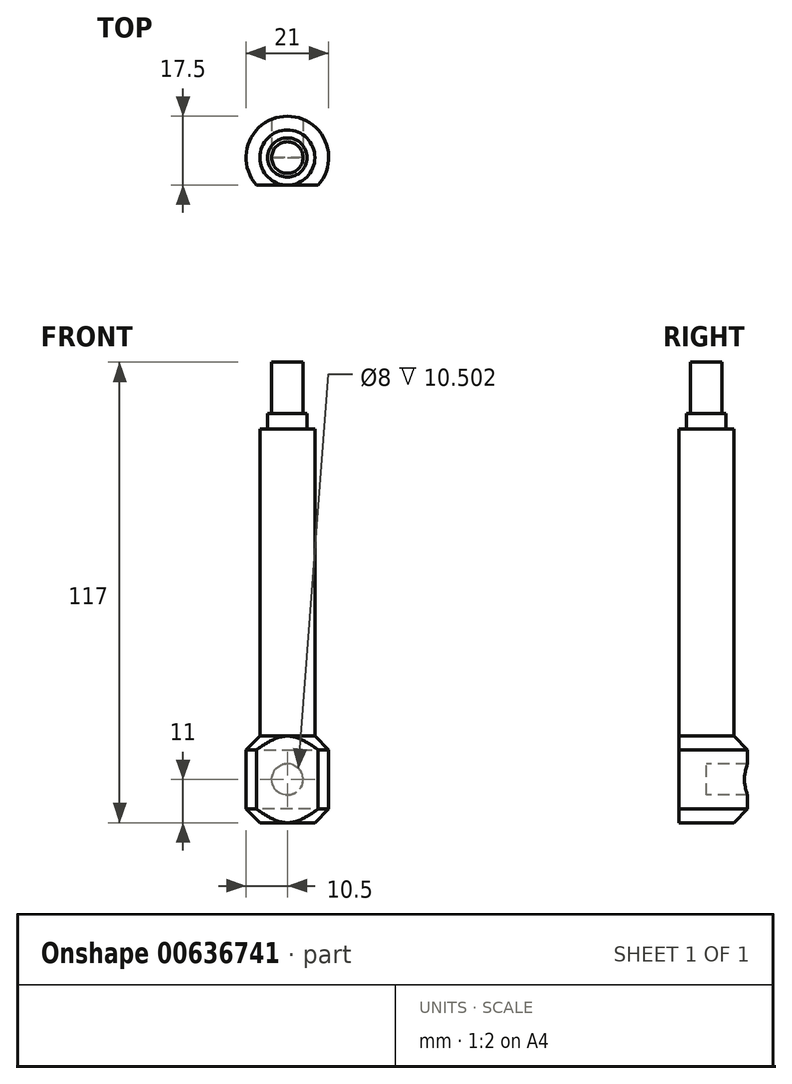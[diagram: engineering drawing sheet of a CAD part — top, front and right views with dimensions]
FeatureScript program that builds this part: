
annotation { "Feature Type Name" : "Feature", "Feature Type Description" : "" }
export const myFeature = defineFeature(function(context is Context, id is Id, definition is map)
    precondition{}
    {
        {
            var Q0;
            Q0=qCreatedBy(makeId("Front.planeOp"),FACE);
            var sketch = newSketch(context, id + "F0", { "sketchPlane" : qUnion([Q0])});
            skLineSegment(sketch, "E0", {"start": v(0, 0) * mm, "end": v(10.5, 0) * mm});
            skLineSegment(sketch, "E1", {"start": v(10.5, 0) * mm, "end": v(10.5, 22) * mm});
            skLineSegment(sketch, "E2", {"start": v(10.5, 22) * mm, "end": v(7, 22) * mm});
            skLineSegment(sketch, "E3", {"start": v(7, 22) * mm, "end": v(7, 100) * mm});
            skLineSegment(sketch, "E4", {"start": v(7, 100) * mm, "end": v(5, 100) * mm});
            skLineSegment(sketch, "E5", {"start": v(5, 100) * mm, "end": v(5, 104) * mm});
            skLineSegment(sketch, "E6", {"start": v(5, 104) * mm, "end": v(4, 104) * mm});
            skLineSegment(sketch, "E7", {"start": v(4, 104) * mm, "end": v(4, 117) * mm});
            skLineSegment(sketch, "E8", {"start": v(4, 117) * mm, "end": v(0, 117) * mm});
            skLineSegment(sketch, "E9", {"start": v(0, 117) * mm, "end": v(0, 0) * mm});
            skLineSegment(sketch, "E10", {"start": v(0, 117) * mm, "end": v(0, 0) * mm, "construction": true});
            skSolve(sketch);
        }
        {
            var Q0;
            Q0=qSketchRegion(id+"F0",true);
            var Q1;
            Q1=sQuery(id+"F0.wireOp",EDGE,"E9");
            revolve(context, id + "F1", {"entities" : qUnion([Q0]), "axis" : qUnion([Q1]), "revolveType" : RevolveType.FULL});
        }
        {
            var Q0;
            Q0=qCreatedBy(makeId("Front.planeOp"),FACE);
            var sketch = newSketch(context, id + "F2", { "sketchPlane" : qUnion([Q0])});
            skLineSegment(sketch, "E11", {"start": v(-10.5, 0) * mm, "end": v(-10.5, 22) * mm, "construction": true});
            skLineSegment(sketch, "E12", {"start": v(10.5, 22) * mm, "end": v(10.5, 0) * mm, "construction": true});
            skLineSegment(sketch, "E13", {"start": v(0, 0) * mm, "end": v(0, 28.11) * mm, "construction": true});
            skLineSegment(sketch, "E14", {"start": v(-10.5, 11) * mm, "end": v(10.5, 11) * mm, "construction": true});
            skPoint(sketch, "E15", {"position": v(0, 11) * mm});
            skSolve(sketch);
        }
        {
            var Q0;
            Q0=sQuery(id+"F2.wireOp",VERTEX,"E15");
            var Q1;
            Q1=makeQuery(id+"F1.opRevolve","SWEPT_BODY",BODY,{"disambiguationData":[OSD([sQuery(id+"F0.wireOp",EDGE,"E0"),sQuery(id+"F0.wireOp",EDGE,"E1"),sQuery(id+"F0.wireOp",EDGE,"E2"),sQuery(id+"F0.wireOp",EDGE,"E3"),sQuery(id+"F0.wireOp",EDGE,"E4"),sQuery(id+"F0.wireOp",EDGE,"E5"),sQuery(id+"F0.wireOp",EDGE,"E6"),sQuery(id+"F0.wireOp",EDGE,"E7"),sQuery(id+"F0.wireOp",EDGE,"E8"),sQuery(id+"F0.wireOp",EDGE,"E9")])]});
            hole(context, id + "F3", {"style" : HoleStyle.SIMPLE, "endStyle" : HoleEndStyle.THROUGH, "holeDiameter" : 8 * mm, "tappedDepth" : 12 * mm, "tapClearance" : 3, "locations" : qUnion([Q0]), "scope" : qUnion([Q1])});
        }
        {
            var Q0;
            Q0=qCreatedBy(makeId("Front.planeOp"),FACE);
            cPlane(context, id + "F4", {"entities" : qUnion([Q0]), "cplaneType" : CPlaneType.OFFSET, "offset" : 7 * mm, "width" : 150 * mm, "height" : 150 * mm});
        }
        {
            var Q0;
            Q0=qCreatedBy(id+"F4.planeOp",FACE);
            var sketch = newSketch(context, id + "F5", { "sketchPlane" : qUnion([Q0])});
            skLineSegment(sketch, "E16.bottom", {"start": v(-12.1, 22) * mm, "end": v(13.39, 22) * mm});
            skLineSegment(sketch, "E16.top", {"start": v(-12.1, 0) * mm, "end": v(13.39, 0) * mm});
            skLineSegment(sketch, "E16.left", {"start": v(-12.1, 22) * mm, "end": v(-12.1, 0) * mm});
            skLineSegment(sketch, "E16.right", {"start": v(13.39, 22) * mm, "end": v(13.39, 0) * mm});
            skLineSegment(sketch, "E17", {"start": v(-7.83, 0) * mm, "end": v(-7.83, 22) * mm, "construction": true});
            skLineSegment(sketch, "E18", {"start": v(7.83, 22) * mm, "end": v(7.83, 0) * mm, "construction": true});
            skLineSegment(sketch, "E19", {"start": v(0, 100) * mm, "end": v(0, 22) * mm, "construction": true});
            skLineSegment(sketch, "E20", {"start": v(-7.83, 0) * mm, "end": v(-7.83, 22) * mm});
            skLineSegment(sketch, "E21", {"start": v(7.83, 22) * mm, "end": v(7.83, 0) * mm});
            skSolve(sketch);
        }
        {
            var Q0;
            Q0=qSketchRegion(id+"F5",true);
            extrude(context, id + "F6", {"entities" : qUnion([Q0]), "operationType" : NewBodyOperationType.REMOVE, "endBound" : BoundingType.THROUGH_ALL, "depth" : 25 * mm});
        }
        {
            var Q0;
            Q0=makeQuery(id+"FCb6IwEKzA1KBKa_1.1.F6.boolean.opBoolean","SPLIT",EDGE,{"disambiguationData":[OD(1.0)],"derivedFrom":makeQuery(id+"F1.opRevolve","SWEPT_EDGE",EDGE,{"disambiguationData":[OSD([sQuery(id+"F0.wireOp",EDGE,"E1"),sQuery(id+"F0.wireOp",EDGE,"E2")])]})});
            var Q1;
            Q1=makeQuery(id+"FCb6IwEKzA1KBKa_1.1.F6.boolean.opBoolean","SPLIT",EDGE,{"disambiguationData":[OD(0.0)],"derivedFrom":makeQuery(id+"F1.opRevolve","SWEPT_EDGE",EDGE,{"disambiguationData":[OSD([sQuery(id+"F0.wireOp",EDGE,"E1"),sQuery(id+"F0.wireOp",EDGE,"E2")])]})});
            var Q2;
            Q2=makeQuery(id+"FCb6IwEKzA1KBKa_1.1.F6.boolean.opBoolean","SPLIT",EDGE,{"disambiguationData":[OD(1.0)],"derivedFrom":makeQuery(id+"F1.opRevolve","SWEPT_EDGE",EDGE,{"disambiguationData":[OSD([sQuery(id+"F0.wireOp",EDGE,"E0"),sQuery(id+"F0.wireOp",EDGE,"E1")])]})});
            var Q3;
            Q3=makeQuery(id+"FCb6IwEKzA1KBKa_1.1.F6.boolean.opBoolean","SPLIT",EDGE,{"disambiguationData":[OD(0.0)],"derivedFrom":makeQuery(id+"F1.opRevolve","SWEPT_EDGE",EDGE,{"disambiguationData":[OSD([sQuery(id+"F0.wireOp",EDGE,"E0"),sQuery(id+"F0.wireOp",EDGE,"E1")])]})});
            chamfer(context, id + "F7", {"entities" : qUnion([Q0, Q1, Q2, Q3]), "width" : 3.5 * mm, "tangentPropagation" : true});
        }
    });
